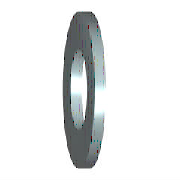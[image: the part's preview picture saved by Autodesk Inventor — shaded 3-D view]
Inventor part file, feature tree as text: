
AUTODESK INVENTOR PART (.ipt)
format: ipt  version: 2021.2 (Build 252289000, 289)  size: 108,032 bytes
history: native  units: mm (DEFAULTED — no unit token found)
features: extrude x1, other x1, plane x1, sketch x1
ambient origin geometry x7: Origin, YZ Plane, XY Plane, X Axis, Y Axis, Z Axis, Center Point
bodies: Solid1 (feature_tree)
feature tree (4):
  extrude  "Базовый элемент"  Depth=4.3mm
  other  "Work Axis1"
  plane  "Work Plane1"
  sketch  "Эскиз"
